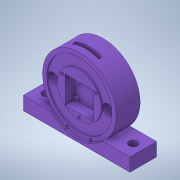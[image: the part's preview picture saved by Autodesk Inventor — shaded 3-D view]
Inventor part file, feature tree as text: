
AUTODESK INVENTOR PART (.ipt)
format: ipt  version: 2020.1 (Build 241239000, 239)  size: 300,032 bytes
history: native  units: in
note: dims shown in document units (in); Inventor stores cm internally (conversion verified against a paired STEP export)
features: sketch x12, extrude x8, hole x6
ambient origin geometry x8: Origin, YZ Plane, XZ Plane, XY Plane, X Axis, Y Axis, Z Axis, Center Point
bodies: Solid1 (feature_tree)
feature tree (26):
  extrude  "Extrusion1"  Depth=0.9in TaperAngle=0.0deg
  extrude  "Extrusion2"  Depth=1.6535in
  extrude  "Extrusion4"  Depth=0.0472in
  extrude  "Extrusion5"  Depth=0.5315in
  extrude  "Extrusion11"  Depth=0.3701in TaperAngle=0.0deg
  extrude  "Extrusion14"  Depth=0.3701in
  extrude  "Extrusion16"  Depth=1.0in TaperAngle=0.0deg
  hole  "Hole for 1/4 0.266 diam"  [1 undecoded]
  hole  "Hole for 1/4 Insert"  [1 undecoded]
  extrude  "Extrusion To Support Camera"  Depth=1.0236in
  hole  "Hole for 2-56 threads for camera"  [1 undecoded]
  hole  "Hole for 2-56 insert"  [1 undecoded]
  hole  "Hole for 6-32 threads for battery holder"  [1 undecoded]
  hole  "Hole20"  [1 undecoded]
  sketch  "Sketch1"  dims[d0=2.7559in d1=0.9in d2=0.0in]
  sketch  "Sketch2"  dims[d3=2.4409in d4=1.6535in]
  sketch  "Sketch7"  dims[d5=0.0472in d6=0.0in d24=0.4119in]
  sketch  "Sketch10"  dims[d25=0.6063in d27=0.5315in]
  sketch  "Sketch20"  dims[d28=0.5315in d31=0.3701in d32=0.0in]
  sketch  "Sketch24"  dims[d33=0.3701in d34=0.4921in]
  sketch  "Sketch27"  dims[d35=0.1339in d36=1.0in d37=0.0in]
  sketch  "Sketch43"  dims[d66=0.164in d76=0.4109in]
  sketch  "Sketch44"  dims[d77=2.0in d78=0.5in]
  sketch  "Sketch45"  dims[d79=0.9in d80=0.0in d95=1.0236in]
  sketch  "Sketch46"  dims[d96=0.3937in d97=0.7874in d99=360.0deg]
  sketch  "Sketch51"  dims[d101=0.2188in d102=0.0in d106=0.1in d107=0.0in d192=0.375in d193=0.375in d194=0.266in d195=0.75in d196=0.507in d197=0.25in d198=0.5635in d199=0.157in d200=0.0in d201=0.316in d202=0.75in d203=0.507in d204=0.25in d205=0.5635in d206=0.312in d207=0.0in d208=0.1063in d209=0.0in d210=0.067in d211=0.172in d212=0.375in d213=0.25in d214=0.5635in d215=0.261in d216=0.0in d217=0.1285in d218=0.172in d219=0.172in d220=0.25in d221=0.5635in d222=0.157in d223=0.0in d224=0.104in d225=0.276in d226=0.191in d227=0.281in d228=0.5635in d229=0.432in d230=0.0in d262=1.4765in d263=1.1811in d265=360.0deg d267=0.104in d268=0.276in d269=0.191in d270=0.281in d271=0.5635in d272=0.432in d273=0.8108in]
note: 6 required parameter values undecoded (feature->parameter linkage not recoverable at this tier; creation-order binding heuristic only, values carry confidence <= 0.55)
